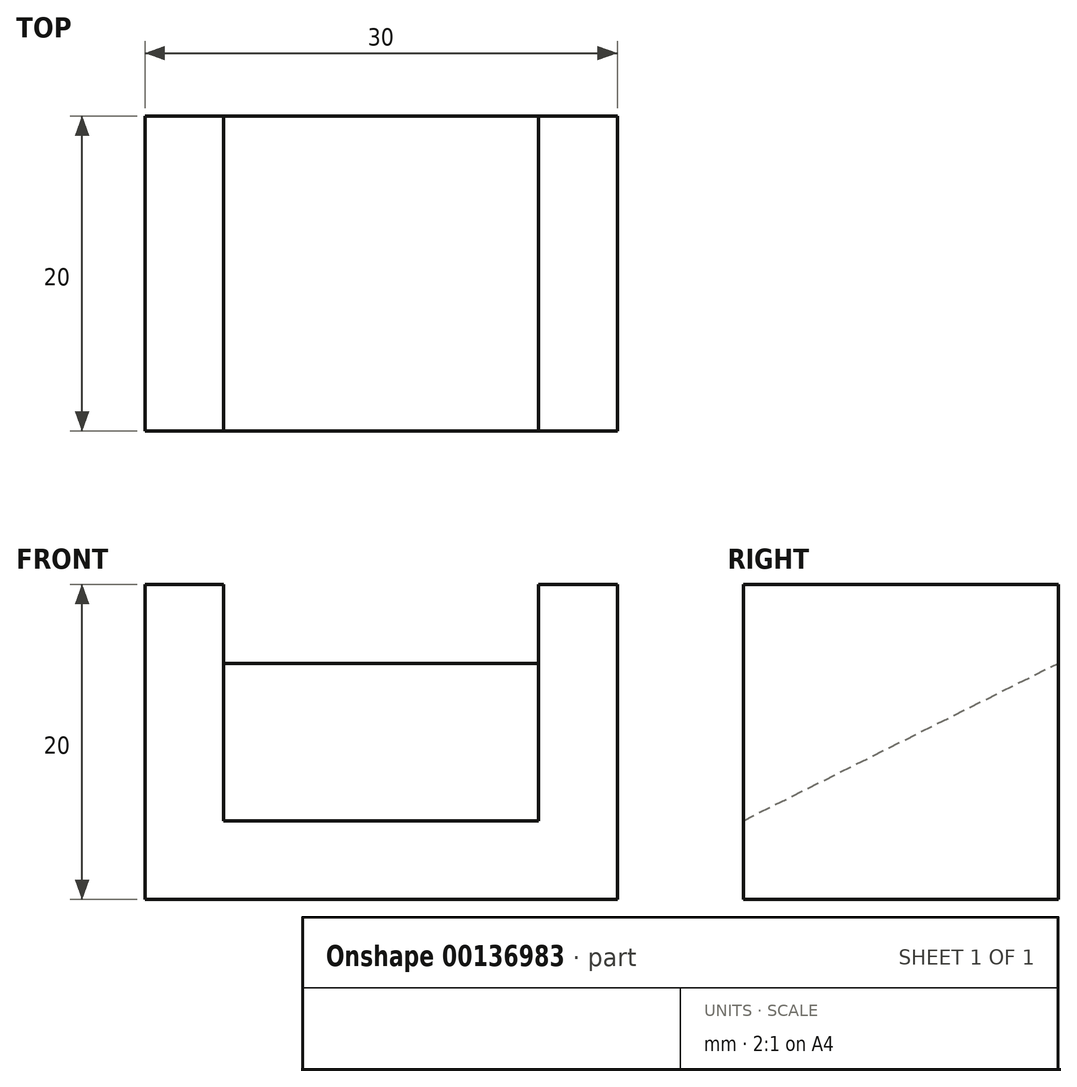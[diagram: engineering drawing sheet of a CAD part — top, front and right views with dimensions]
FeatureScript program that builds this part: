
annotation { "Feature Type Name" : "Feature", "Feature Type Description" : "" }
export const myFeature = defineFeature(function(context is Context, id is Id, definition is map)
    precondition{}
    {
        {
            var Q0;
            Q0=qCreatedBy(makeId("Front.planeOp"),FACE);
            var sketch = newSketch(context, id + "F0", { "sketchPlane" : qUnion([Q0])});
            skLineSegment(sketch, "E0.bottom", {"start": v(-15, 0) * mm, "end": v(15, 0) * mm});
            skLineSegment(sketch, "E0.top", {"start": v(-15, 20) * mm, "end": v(15, 20) * mm});
            skLineSegment(sketch, "E0.left", {"start": v(-15, 0) * mm, "end": v(-15, 20) * mm});
            skLineSegment(sketch, "E0.right", {"start": v(15, 0) * mm, "end": v(15, 20) * mm});
            skSolve(sketch);
        }
        {
            var Q0;
            Q0 = qSketchRegion(id + "F0", true);
            extrude(context, id + "F1", {"entities" : qUnion([Q0]), "endBound" : BoundingType.SYMMETRIC, "depth" : 20 * mm});
        }
        {
            var Q0;
            Q0=qCreatedBy(makeId("Right.planeOp"),FACE);
            var sketch = newSketch(context, id + "F2", { "sketchPlane" : qUnion([Q0])});
            skLineSegment(sketch, "E1", {"start": v(-10, 20) * mm, "end": v(10, 20) * mm});
            skLineSegment(sketch, "E2", {"start": v(-10, 20) * mm, "end": v(-10, 5) * mm});
            skLineSegment(sketch, "E3", {"start": v(10, 20) * mm, "end": v(10, 15) * mm});
            skLineSegment(sketch, "E4", {"start": v(-10, 5) * mm, "end": v(10, 15) * mm});
            skSolve(sketch);
        }
        {
            var Q0;
            Q0 = qSketchRegion(id + "F2", true);
            extrude(context, id + "F3", {"entities" : qUnion([Q0]), "operationType" : NewBodyOperationType.REMOVE, "endBound" : BoundingType.SYMMETRIC, "oppositeDirection" : true, "depth" : 20 * mm});
        }
    });
